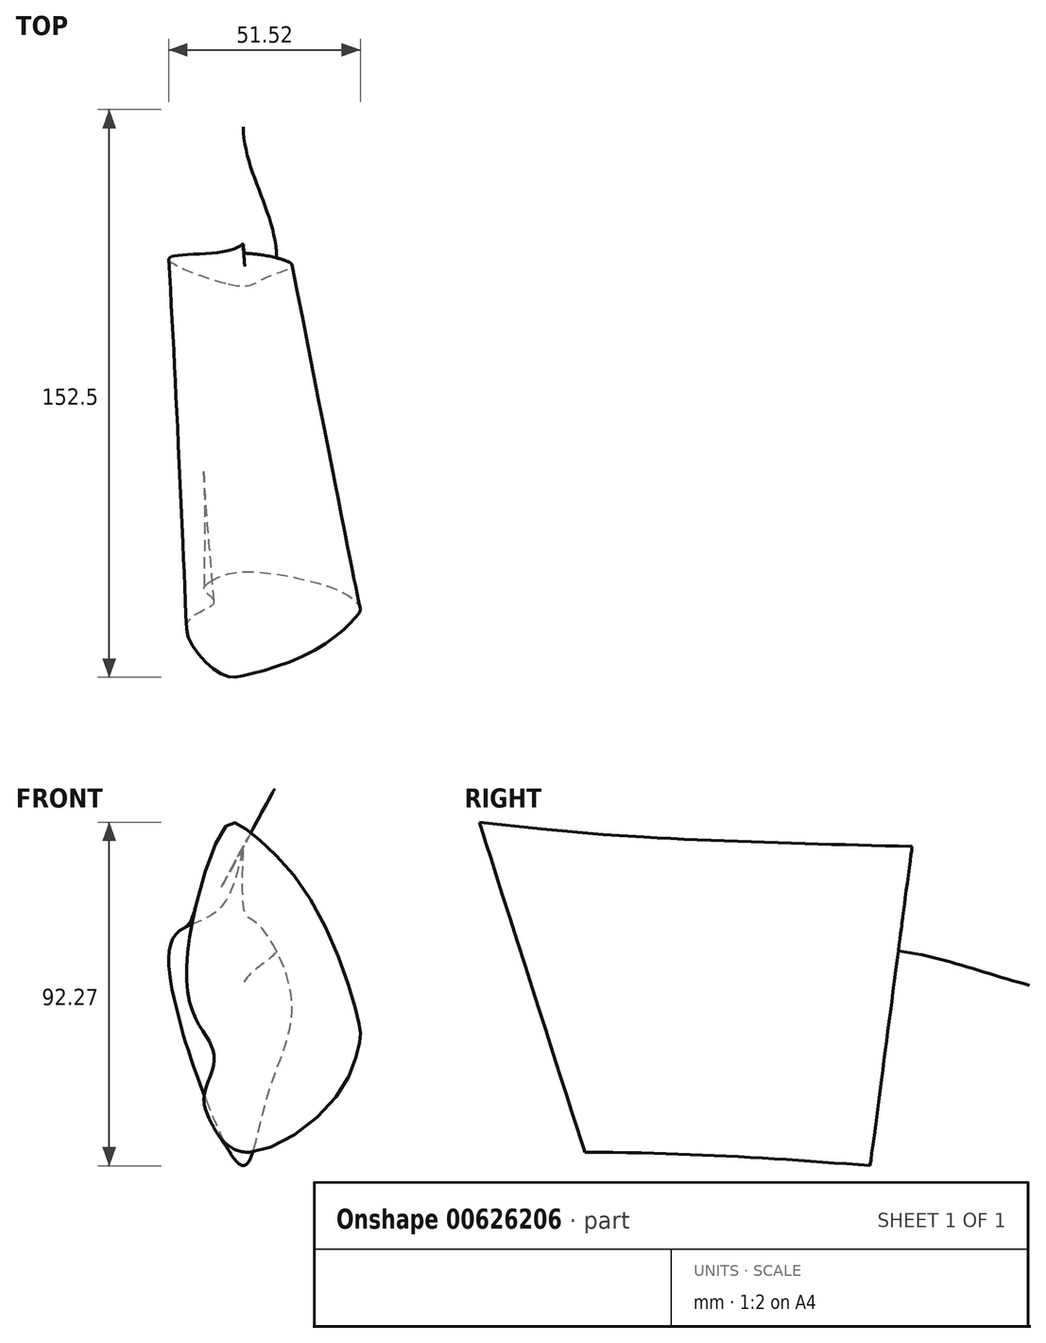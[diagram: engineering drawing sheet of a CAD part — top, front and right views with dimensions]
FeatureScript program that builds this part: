
annotation { "Feature Type Name" : "Feature", "Feature Type Description" : "" }
export const myFeature = defineFeature(function(context is Context, id is Id, definition is map)
    precondition{}
    {
        {
            var Q0;
            Q0=qCreatedBy(makeId("Right.planeOp"),FACE);
            var sketch = newSketch(context, id + "F0", { "sketchPlane" : qUnion([Q0])});
            skFitSpline(sketch, "E0", {"points": [v(-5.51, -51.71) * mm, v(-42.79, -42.79) * mm, v(-56.79, -29.31) * mm, v(-75.51, -22.66) * mm, v(-88.64, 0) * mm, v(-67.81, 34.74) * mm, v(-19.69, 45.24) * mm, v(46.46, 39.11) * mm, v(69.11, 24.15) * mm, v(88.64, -3.06) * mm, v(87.41, -36.14) * mm, v(40.69, -52.06) * mm, v(-5.51, -51.71) * mm]});
            skLineSegment(sketch, "E1", {"start": v(-65.01, 58.89) * mm, "end": v(-25.81, -63.79) * mm});
            skLineSegment(sketch, "E2", {"start": v(59.41, 51.54) * mm, "end": v(44.01, -65.71) * mm});
            skSolve(sketch);
        }
        {
            var Q0;
            Q0=sQuery(id+"F0.wireOp",EDGE,"E1");
            cPlane(context, id + "F1", {"entities" : qUnion([Q0]), "cplaneType" : CPlaneType.LINE_ANGLE, "offset" : 25 * mm, "angle" : 90 * degree, "width" : 150 * mm, "height" : 150 * mm});
        }
        {
            var Q0;
            Q0=sQuery(id+"F0.wireOp",EDGE,"E2");
            cPlane(context, id + "F2", {"entities" : qUnion([Q0]), "cplaneType" : CPlaneType.LINE_ANGLE, "offset" : 25 * mm, "angle" : 90 * degree, "width" : 150 * mm, "height" : 150 * mm});
        }
        {
            var Q0;
            Q0=qCreatedBy(id+"F1.planeOp",FACE);
            var sketch = newSketch(context, id + "F3", { "sketchPlane" : qUnion([Q0])});
            skFitSpline(sketch, "E3", {"points": [v(8.88, -27.45) * mm, v(0, -36.18) * mm, v(-25.33, -20.17) * mm, v(-31.38, -4.03) * mm, v(-31.13, 0) * mm, v(-18.32, 34.72) * mm, v(0, 55.42) * mm, v(4.4, 56) * mm, v(15.18, 10.63) * mm, v(9.1, -5.05) * mm, v(8, -11.58) * mm, v(10.5, -20.17) * mm, v(8.88, -27.45) * mm]});
            skSolve(sketch);
        }
        {
            var Q0;
            Q0=qCreatedBy(id+"F2.planeOp",FACE);
            var sketch = newSketch(context, id + "F4", { "sketchPlane" : qUnion([Q0])});
            skFitSpline(sketch, "E4", {"points": [v(5.47, 25.58) * mm, v(18.26, 17.52) * mm, v(18.57, 0) * mm, v(11.49, -23.35) * mm, v(0, -45.13) * mm, v(-6.35, -26.7) * mm, v(-13.02, 0) * mm, v(-3.48, 20.67) * mm, v(-0.35, 23.7) * mm, v(0, 41.35) * mm, v(5.47, 25.58) * mm]});
            skSolve(sketch);
        }
        {
            var Q0;
            {var subQ0=sQuery(id+"F0.wireOp",EDGE,"E1");var subQ1=sQuery(id+"F0.wireOp",EDGE,"E0");var subQ2=makeQuery(id+"F0.imprint","INTERSECT",VERTEX,{"disambiguationData":[OD(0.0)],"derivedFrom":[subQ1,subQ0]});Q0=makeQuery(id+"F0.imprint","IMPRINT",FACE,{"disambiguationData":[TD([[makeQuery(id+"F0.imprint","IMPRINT",EDGE,{"disambiguationData":[TD([[subQ2,-1.0]])],"derivedFrom":subQ1}),-1.0]])]});}
            var sketch = newSketch(context, id + "F5", { "sketchPlane" : qUnion([Q0])});
            skFitSpline(sketch, "E5.0", {"points": [v(-5.51, -51.71) * mm, v(-19.38, -50.5) * mm, v(-44.83, -47.32) * mm, v(-54.65, -26.16) * mm, v(-77.61, -26.2) * mm, v(-95.99, 0.86) * mm, v(-69.35, 42.44) * mm, v(-20.69, 46.52) * mm, v(47.7, 43.7) * mm, v(69.18, 24.96) * mm, v(91.91, -0.75) * mm, v(95.86, -43.7) * mm, v(38.2, -54.13) * mm, v(9.7, -53.04) * mm, v(-5.51, -51.71) * mm]});
            skLineSegment(sketch, "E5.1", {"start": v(-65.01, 58.89) * mm, "end": v(-25.81, -63.79) * mm});
            skLineSegment(sketch, "E5.2", {"start": v(59.41, 51.54) * mm, "end": v(44.01, -65.71) * mm});
            skSolve(sketch);
        }
        {
            var Q0;
            Q0=makeQuery(id+"F3.imprint","IMPRINT",FACE,{"disambiguationData":[TD([[makeQuery(id+"F3.imprint","IMPRINT",EDGE,{"derivedFrom":sQuery(id+"F3.wireOp",EDGE,"E3")}),-1.0]])]});
            var Q1;
            Q1=makeQuery(id+"F4.imprint","IMPRINT",FACE,{"disambiguationData":[TD([[makeQuery(id+"F4.imprint","IMPRINT",EDGE,{"derivedFrom":sQuery(id+"F4.wireOp",EDGE,"E4")}),-1.0]])]});
            var Q2;
            Q2=sQuery(id+"F5.wireOp",EDGE,"E5.0");
            loft(context, id + "F6", {"sheetProfilesArray" : [{ "sheetProfileEntities" : qUnion([Q0]) }, { "sheetProfileEntities" : qUnion([Q1]) }], "guidesArray" : [{ "guideEntities" : qUnion([Q2]), "guideDerivativeType" : LoftGuideDerivativeType.DEFAULT, "guideDerivativeMagnitude" : 1 }]});
        }
        {
            var Q1;
            Q1=makeQuery(id+"F6.opLoft","CAP_FACE",FACE,{"disambiguationData":[OSD([makeQuery(id+"F4.imprint","IMPRINT",FACE,{"disambiguationData":[TD([[makeQuery(id+"F4.imprint","IMPRINT",EDGE,{"derivedFrom":sQuery(id+"F4.wireOp",EDGE,"E4")}),-1.0]])]})])],"isStart":true});
            var Q2;
            Q2=sQuery(id+"F0.wireOp",VERTEX,"E0.9.internal");
            loft(context, id + "F7", {"operationType" : NewBodyOperationType.ADD, "startCondition" : LoftEndDerivativeType.NORMAL_TO_PROFILE, "startMagnitude" : 1, "endCondition" : LoftEndDerivativeType.TANGENT_TO_PROFILE, "endMagnitude" : 1, "sheetProfilesArray" : [{ "sheetProfileEntities" : qUnion([Q1]) }, { "sheetProfileEntities" : qUnion([Q2]) }]});
        }
    });
